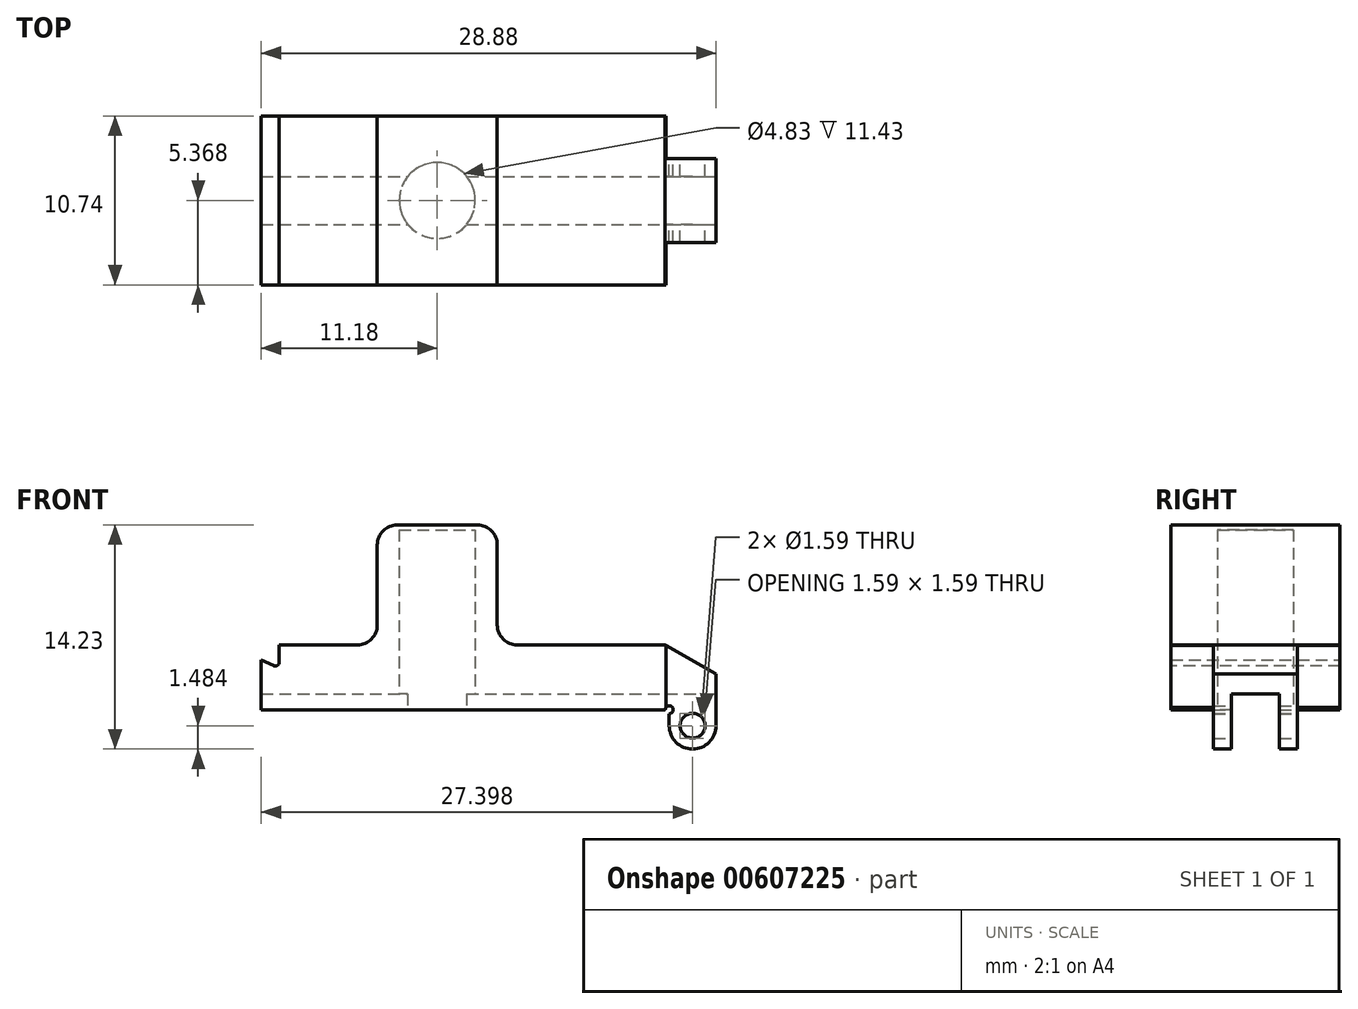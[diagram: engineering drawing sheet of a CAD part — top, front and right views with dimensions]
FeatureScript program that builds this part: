
annotation { "Feature Type Name" : "Feature", "Feature Type Description" : "" }
export const myFeature = defineFeature(function(context is Context, id is Id, definition is map)
    precondition{}
    {
        {
            var Q0;
            Q0=qCreatedBy(makeId("Front.planeOp"),FACE);
            var sketch = newSketch(context, id + "F0", { "sketchPlane" : qUnion([Q0])});
            skLineSegment(sketch, "E0", {"start": v(-11.18, 0) * mm, "end": v(14.73, 0) * mm});
            skLineSegment(sketch, "E1", {"start": v(14.73, 0) * mm, "end": v(14.73, -1.02) * mm});
            skArc(sketch, "E2", {"start": v(14.73, -1.02) * mm, "mid": v(16.22, -2.5) * mm, "end": v(17.7, -1.02) * mm});
            skLineSegment(sketch, "E3", {"start": v(17.7, -1.02) * mm, "end": v(17.7, 2.29) * mm});
            skLineSegment(sketch, "E4", {"start": v(17.7, 2.29) * mm, "end": v(14.47, 4.11) * mm});
            skLineSegment(sketch, "E5", {"start": v(-10.03, 4.11) * mm, "end": v(-10.03, 2.62) * mm});
            skLineSegment(sketch, "E6", {"start": v(-10.03, 2.62) * mm, "end": v(-11.18, 3.18) * mm});
            skLineSegment(sketch, "E7", {"start": v(-11.18, 3.18) * mm, "end": v(-11.18, 0) * mm});
            skCircle(sketch, "E8", {"center": v(16.22, -1.02) * mm, "radius": 0.8 * mm});
            skLineSegment(sketch, "E9", {"start": v(-10.03, 4.11) * mm, "end": v(-3.81, 4.11) * mm});
            skLineSegment(sketch, "E10", {"start": v(-3.81, 4.11) * mm, "end": v(-3.81, 11.73) * mm});
            skLineSegment(sketch, "E11", {"start": v(-3.81, 11.73) * mm, "end": v(3.8, 11.73) * mm});
            skLineSegment(sketch, "E12", {"start": v(3.8, 11.73) * mm, "end": v(3.81, 4.11) * mm});
            skLineSegment(sketch, "E13", {"start": v(3.81, 4.11) * mm, "end": v(14.47, 4.11) * mm});
            skLineSegment(sketch, "E14", {"start": v(-3.81, 4.11) * mm, "end": v(0, 4.11) * mm, "construction": true});
            skLineSegment(sketch, "E15", {"start": v(0, 4.11) * mm, "end": v(3.81, 4.11) * mm, "construction": true});
            skArc(sketch, "E16", {"start": v(14.48, 0) * mm, "mid": v(14.91, 0.18) * mm, "end": v(14.73, -0.25) * mm});
            skSolve(sketch);
        }
        {
            var Q0;
            {var subQ3=sQuery(id+"F0.wireOp",EDGE,"E2");Q0=makeQuery(id+"F0.imprint","IMPRINT",FACE,{"disambiguationData":[TD([[makeQuery(id+"F0.imprint","IMPRINT",EDGE,{"derivedFrom":subQ3}),1.0]])]});}
            extrude(context, id + "F1", {"entities" : qUnion([Q0]), "depth" : 10.74 * mm, "offsetDistance" : 25.4 * mm});
        }
        {
            var Q0;
            Q0=makeQuery(id+"F1.opExtrude","SWEPT_FACE",FACE,{"disambiguationData":[OSD([sQuery(id+"F0.wireOp",EDGE,"E3")])]});
            var sketch = newSketch(context, id + "F2", { "sketchPlane" : qUnion([Q0])});
            skLineSegment(sketch, "E17.0", {"start": v(-10.74, 4.11) * mm, "end": v(0, 4.11) * mm, "construction": true});
            skLineSegment(sketch, "E18.0.0", {"start": v(0, -1.02) * mm, "end": v(0, -2.5) * mm, "construction": true});
            skLineSegment(sketch, "E18.0.2", {"start": v(-10.74, -1.02) * mm, "end": v(-10.74, -2.5) * mm, "construction": true});
            skLineSegment(sketch, "E19.bottom", {"start": v(-10.74, -2.5) * mm, "end": v(-8.04, -2.5) * mm});
            skLineSegment(sketch, "E19.top", {"start": v(-10.74, 4.11) * mm, "end": v(-8.04, 4.11) * mm});
            skLineSegment(sketch, "E19.left", {"start": v(-10.74, -2.5) * mm, "end": v(-10.74, 4.11) * mm});
            skLineSegment(sketch, "E19.right", {"start": v(-8.04, -2.5) * mm, "end": v(-8.04, 4.11) * mm});
            skLineSegment(sketch, "E20.bottom", {"start": v(0, -2.5) * mm, "end": v(-2.7, -2.5) * mm});
            skLineSegment(sketch, "E20.top", {"start": v(0, 4.11) * mm, "end": v(-2.7, 4.11) * mm});
            skLineSegment(sketch, "E20.left", {"start": v(0, -2.5) * mm, "end": v(0, 4.11) * mm});
            skLineSegment(sketch, "E20.right", {"start": v(-2.7, -2.5) * mm, "end": v(-2.7, 4.11) * mm});
            skSolve(sketch);
        }
        {
            var Q0;
            {var subQ0=sQuery(id+"F2.wireOp",EDGE,"E19.top");Q0=makeQuery(id+"F2.imprint","IMPRINT",FACE,{"disambiguationData":[TD([[makeQuery(id+"F2.imprint","IMPRINT",EDGE,{"derivedFrom":subQ0}),-1.0]])]});}
            var Q1;
            {var subQ0=sQuery(id+"F2.wireOp",EDGE,"E19.left");var subQ1=sQuery(id+"F0.wireOp",EDGE,"E3");var subQ2=makeQuery(id+"F1.opExtrude","SWEPT_EDGE",EDGE,{"disambiguationData":[OSD([sQuery(id+"F0.wireOp",EDGE,"E2"),subQ1])]});var subQ3=makeQuery(id+"F2.imprint","INTERSECT",VERTEX,{"derivedFrom":[subQ2,subQ0]});Q1=makeQuery(id+"F2.imprint","IMPRINT",FACE,{"disambiguationData":[TD([[makeQuery(id+"F2.imprint","IMPRINT",EDGE,{"disambiguationData":[TD([[subQ3,-1.0]])],"derivedFrom":subQ0}),-1.0]])]});}
            var Q2;
            {var subQ0=sQuery(id+"F2.wireOp",EDGE,"E19.bottom");Q2=makeQuery(id+"F2.imprint","IMPRINT",FACE,{"disambiguationData":[TD([[makeQuery(id+"F2.imprint","IMPRINT",EDGE,{"derivedFrom":subQ0}),1.0]])]});}
            var Q3;
            {var subQ0=sQuery(id+"F2.wireOp",EDGE,"E20.top");Q3=makeQuery(id+"F2.imprint","IMPRINT",FACE,{"disambiguationData":[TD([[makeQuery(id+"F2.imprint","IMPRINT",EDGE,{"derivedFrom":subQ0}),1.0]])]});}
            var Q4;
            {var subQ0=sQuery(id+"F2.wireOp",EDGE,"E20.left");var subQ1=sQuery(id+"F0.wireOp",EDGE,"E3");var subQ2=makeQuery(id+"F1.opExtrude","SWEPT_EDGE",EDGE,{"disambiguationData":[OSD([sQuery(id+"F0.wireOp",EDGE,"E2"),subQ1])]});var subQ3=makeQuery(id+"F2.imprint","INTERSECT",VERTEX,{"derivedFrom":[subQ2,subQ0]});Q4=makeQuery(id+"F2.imprint","IMPRINT",FACE,{"disambiguationData":[TD([[makeQuery(id+"F2.imprint","IMPRINT",EDGE,{"disambiguationData":[TD([[subQ3,-1.0]])],"derivedFrom":subQ0}),1.0]])]});}
            var Q5;
            {var subQ0=sQuery(id+"F2.wireOp",EDGE,"E20.bottom");Q5=makeQuery(id+"F2.imprint","IMPRINT",FACE,{"disambiguationData":[TD([[makeQuery(id+"F2.imprint","IMPRINT",EDGE,{"derivedFrom":subQ0}),-1.0]])]});}
            extrude(context, id + "F3", {"entities" : qUnion([Q0, Q1, Q2, Q3, Q4, Q5]), "operationType" : NewBodyOperationType.REMOVE, "oppositeDirection" : true, "depth" : 3.17 * mm, "offsetDistance" : 25.4 * mm});
        }
        {
            var Q0;
            Q0=makeQuery(id+"F1.opExtrude","SWEPT_FACE",FACE,{"disambiguationData":[OSD([sQuery(id+"F0.wireOp",EDGE,"E0")])]});
            var sketch = newSketch(context, id + "F4", { "sketchPlane" : qUnion([Q0])});
            skCircle(sketch, "E21", {"center": v(0, 5.37) * mm, "radius": 2.41 * mm});
            skLineSegment(sketch, "E22", {"start": v(0, 0) * mm, "end": v(0, 10.74) * mm, "construction": true});
            skSolve(sketch);
        }
        {
            var Q0;
            Q0 = qSketchRegion(id + "F4", true);
            extrude(context, id + "F5", {"entities" : qUnion([Q0]), "operationType" : NewBodyOperationType.REMOVE, "oppositeDirection" : true, "depth" : 11.43 * mm, "offsetDistance" : 25.4 * mm});
        }
        {
            var Q0;
            Q0=makeQuery(id+"F1.opExtrude","SWEPT_EDGE",EDGE,{"disambiguationData":[OSD([sQuery(id+"F0.wireOp",EDGE,"E9"),sQuery(id+"F0.wireOp",EDGE,"E10")])]});
            var Q1;
            Q1=makeQuery(id+"F1.opExtrude","SWEPT_EDGE",EDGE,{"disambiguationData":[OSD([sQuery(id+"F0.wireOp",EDGE,"E12"),sQuery(id+"F0.wireOp",EDGE,"E13")])]});
            var Q2;
            Q2=makeQuery(id+"F1.opExtrude","SWEPT_EDGE",EDGE,{"disambiguationData":[OSD([sQuery(id+"F0.wireOp",EDGE,"E10"),sQuery(id+"F0.wireOp",EDGE,"E11")])]});
            var Q3;
            Q3=makeQuery(id+"F1.opExtrude","SWEPT_EDGE",EDGE,{"disambiguationData":[OSD([sQuery(id+"F0.wireOp",EDGE,"E11"),sQuery(id+"F0.wireOp",EDGE,"E12")])]});
            fillet(context, id + "F6", {"entities" : qUnion([Q0, Q1, Q2, Q3]), "radius" : 1.27 * mm, "tangentPropagation" : true, "allowEdgeOverflow" : false});
        }
        {
            var Q0;
            Q0=makeQuery(id+"F1.opExtrude","SWEPT_EDGE",EDGE,{"disambiguationData":[OSD([sQuery(id+"F0.wireOp",EDGE,"E5"),sQuery(id+"F0.wireOp",EDGE,"E6")])]});
            fillet(context, id + "F7", {"entities" : qUnion([Q0]), "radius" : 0.25 * mm, "tangentPropagation" : true, "allowEdgeOverflow" : false});
        }
        {
            var Q0;
            Q0=makeQuery(id+"F1.opExtrude","SWEPT_FACE",FACE,{"disambiguationData":[OSD([sQuery(id+"F0.wireOp",EDGE,"E3")])]});
            var sketch = newSketch(context, id + "F8", { "sketchPlane" : qUnion([Q0])});
            skLineSegment(sketch, "E23.0.0", {"start": v(-2.7, -1.02) * mm, "end": v(-2.7, -2.5) * mm, "construction": true});
            skLineSegment(sketch, "E23.0.1", {"start": v(-2.7, -1.02) * mm, "end": v(-8.04, -1.02) * mm, "construction": true});
            skLineSegment(sketch, "E23.0.2", {"start": v(-8.04, -1.02) * mm, "end": v(-8.04, -2.5) * mm, "construction": true});
            skLineSegment(sketch, "E24.bottom", {"start": v(-6.9, 1.02) * mm, "end": v(-3.85, 1.02) * mm});
            skLineSegment(sketch, "E24.top", {"start": v(-6.9, -2.5) * mm, "end": v(-3.85, -2.5) * mm});
            skLineSegment(sketch, "E24.left", {"start": v(-6.9, 1.02) * mm, "end": v(-6.9, -2.5) * mm});
            skLineSegment(sketch, "E24.right", {"start": v(-3.85, 1.02) * mm, "end": v(-3.85, -2.5) * mm});
            skLineSegment(sketch, "E25", {"start": v(-8.04, -2.5) * mm, "end": v(-6.9, -2.5) * mm, "construction": true});
            skLineSegment(sketch, "E26", {"start": v(-3.85, -2.5) * mm, "end": v(-2.7, -2.5) * mm, "construction": true});
            skSolve(sketch);
        }
        {
            var Q0;
            {var subQ0=sQuery(id+"F8.wireOp",EDGE,"E24.bottom");Q0=makeQuery(id+"F8.imprint","IMPRINT",FACE,{"disambiguationData":[TD([[makeQuery(id+"F8.imprint","IMPRINT",EDGE,{"derivedFrom":subQ0}),-1.0]])]});}
            var Q1;
            {var subQ0=sQuery(id+"F8.wireOp",EDGE,"E24.top");Q1=makeQuery(id+"F8.imprint","IMPRINT",FACE,{"disambiguationData":[TD([[makeQuery(id+"F8.imprint","IMPRINT",EDGE,{"derivedFrom":subQ0}),1.0]])]});}
            extrude(context, id + "F9", {"entities" : qUnion([Q0, Q1]), "operationType" : NewBodyOperationType.REMOVE, "endBound" : BoundingType.THROUGH_ALL, "oppositeDirection" : true, "depth" : 25.4 * mm, "offsetDistance" : 25.4 * mm});
        }
    });
